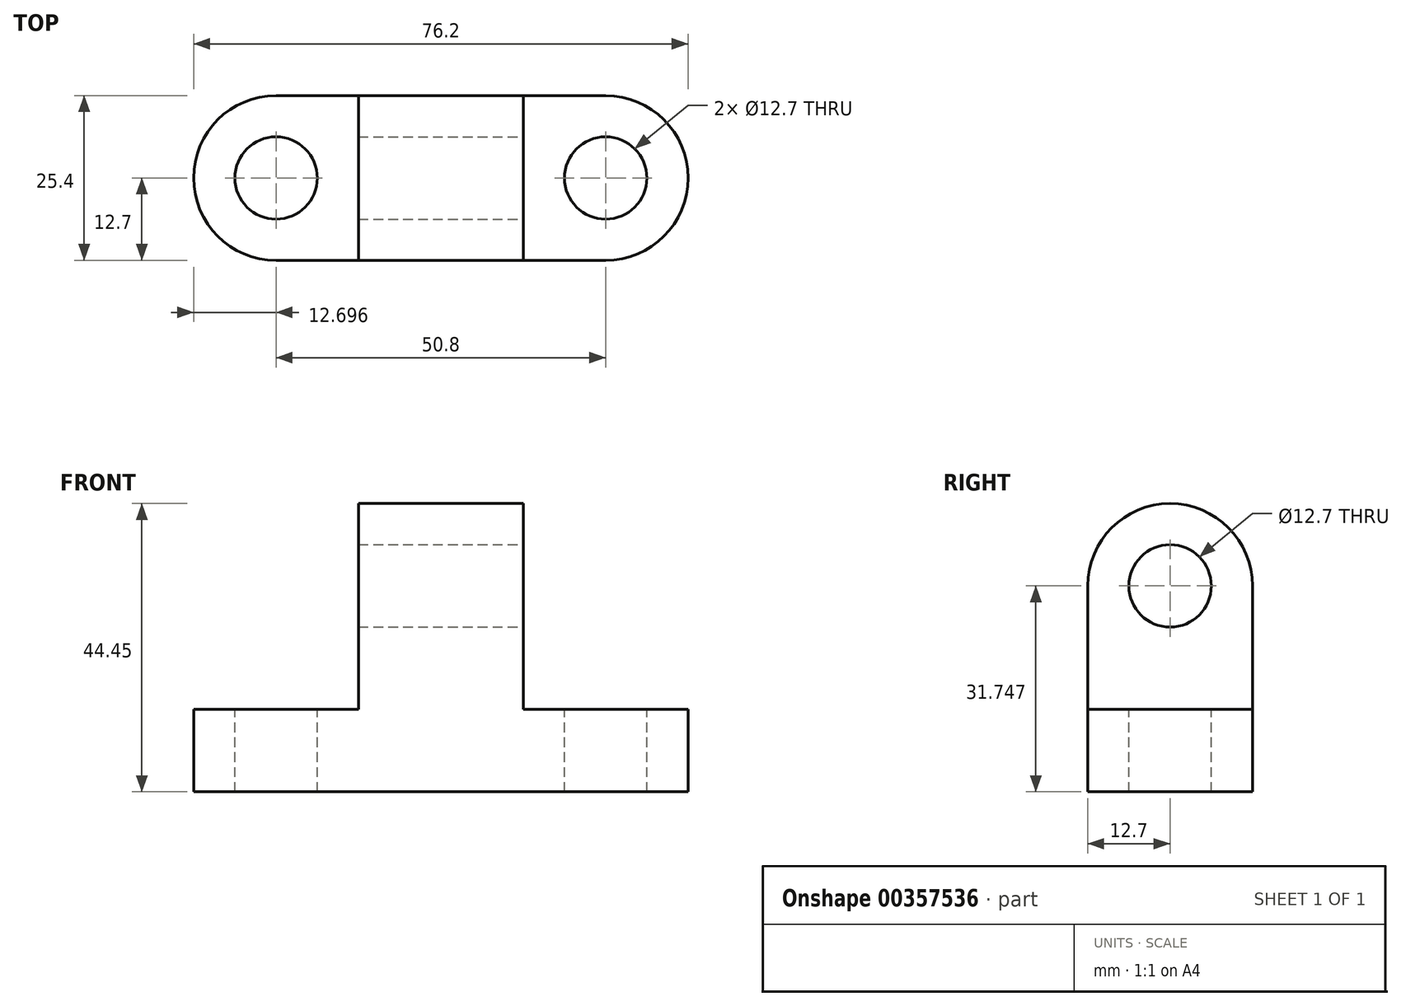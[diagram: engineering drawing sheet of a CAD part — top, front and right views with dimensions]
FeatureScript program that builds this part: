
annotation { "Feature Type Name" : "Feature", "Feature Type Description" : "" }
export const myFeature = defineFeature(function(context is Context, id is Id, definition is map)
    precondition{}
    {
        {
            var Q0;
            Q0=qCreatedBy(makeId("Front.planeOp"),FACE);
            var sketch = newSketch(context, id + "F0", { "sketchPlane" : qUnion([Q0])});
            skLineSegment(sketch, "E0", {"start": v(-50.66, -15.43) * mm, "end": v(-50.66, -28.13) * mm});
            skLineSegment(sketch, "E1", {"start": v(-50.66, -28.13) * mm, "end": v(0.14, -28.13) * mm});
            skLineSegment(sketch, "E2", {"start": v(0.14, -28.13) * mm, "end": v(0.14, -15.43) * mm});
            skLineSegment(sketch, "E3", {"start": v(0.14, -15.43) * mm, "end": v(-12.56, -15.43) * mm});
            skLineSegment(sketch, "E4", {"start": v(-12.56, -15.43) * mm, "end": v(-12.56, 3.62) * mm});
            skLineSegment(sketch, "E5", {"start": v(-12.56, 3.62) * mm, "end": v(-37.96, 3.62) * mm});
            skLineSegment(sketch, "E6", {"start": v(-37.96, 3.62) * mm, "end": v(-37.96, -15.43) * mm});
            skLineSegment(sketch, "E7", {"start": v(-37.96, -15.43) * mm, "end": v(-50.66, -15.43) * mm});
            skSolve(sketch);
        }
        {
            var Q0;
            Q0=makeQuery(id+"F0.imprint","IMPRINT",FACE,{"disambiguationData":[TD([[makeQuery(id+"F0.imprint","IMPRINT",EDGE,{"derivedFrom":sQuery(id+"F0.wireOp",EDGE,"E0")}),1.0]])]});
            extrude(context, id + "F1", {"entities" : qUnion([Q0]), "depth" : 25.4 * mm});
        }
        {
            var Q0;
            Q0=makeQuery(id+"F1.opExtrude","SWEPT_FACE",FACE,{"disambiguationData":[OSD([sQuery(id+"F0.wireOp",EDGE,"E7")])]});
            var sketch = newSketch(context, id + "F2", { "sketchPlane" : qUnion([Q0])});
            skLineSegment(sketch, "E8", {"start": v(0.14, 0) * mm, "end": v(0.14, -12.7) * mm});
            skLineSegment(sketch, "E9", {"start": v(0.14, -12.7) * mm, "end": v(0.14, -25.4) * mm});
            skLineSegment(sketch, "E10", {"start": v(0.14, -12.7) * mm, "end": v(12.84, -12.7) * mm});
            skArc(sketch, "E11", {"start": v(0.14, -25.4) * mm, "mid": v(12.84, -12.7) * mm, "end": v(0.14, 0) * mm});
            skLineSegment(sketch, "E12", {"start": v(-50.66, 0) * mm, "end": v(-50.66, -12.7) * mm});
            skLineSegment(sketch, "E13", {"start": v(-50.66, -12.7) * mm, "end": v(-50.66, -25.4) * mm});
            skLineSegment(sketch, "E14", {"start": v(-50.66, -12.7) * mm, "end": v(-63.36, -12.7) * mm});
            skArc(sketch, "E15", {"start": v(-50.66, 0) * mm, "mid": v(-63.36, -12.7) * mm, "end": v(-50.66, -25.4) * mm});
            skSolve(sketch);
        }
        {
            var Q0;
            Q0 = qSketchRegion(id + "F2", true);
            extrude(context, id + "F3", {"entities" : qUnion([Q0]), "operationType" : NewBodyOperationType.ADD, "oppositeDirection" : true, "depth" : 12.7 * mm});
        }
        {
            var Q0;
            Q0=makeQuery(id+"F1.opExtrude","SWEPT_FACE",FACE,{"disambiguationData":[OSD([sQuery(id+"F0.wireOp",EDGE,"E4")])]});
            var sketch = newSketch(context, id + "F4", { "sketchPlane" : qUnion([Q0])});
            skLineSegment(sketch, "E16", {"start": v(-25.4, 3.62) * mm, "end": v(-12.7, 3.62) * mm});
            skLineSegment(sketch, "E17", {"start": v(-12.7, 3.62) * mm, "end": v(0, 3.62) * mm});
            skLineSegment(sketch, "E18", {"start": v(-12.7, 3.62) * mm, "end": v(-12.7, 16.32) * mm});
            skArc(sketch, "E19", {"start": v(0, 3.62) * mm, "mid": v(-12.7, 16.32) * mm, "end": v(-25.4, 3.62) * mm});
            skSolve(sketch);
        }
        {
            var Q0;
            Q0 = qSketchRegion(id + "F4", true);
            extrude(context, id + "F5", {"entities" : qUnion([Q0]), "operationType" : NewBodyOperationType.ADD, "oppositeDirection" : true, "depth" : 25.4 * mm});
        }
        {
            var Q0;
            Q0=makeQuery(id+"F5.boolean.opBoolean","MERGE",FACE,{"derivedFrom":[makeQuery(id+"F1.opExtrude","SWEPT_FACE",FACE,{"disambiguationData":[OSD([sQuery(id+"F0.wireOp",EDGE,"E4")])]}),makeQuery(id+"F5.opExtrude","CAP_FACE",FACE,{"disambiguationData":[OSD([sQuery(id+"F4.wireOp",EDGE,"E16"),sQuery(id+"F4.wireOp",EDGE,"E17"),sQuery(id+"F4.wireOp",EDGE,"E19")])],"isStart":true})]});
            var sketch = newSketch(context, id + "F6", { "sketchPlane" : qUnion([Q0])});
            skLineSegment(sketch, "E20", {"start": v(-12.7, 16.32) * mm, "end": v(-12.7, 9.97) * mm});
            skPoint(sketch, "E20.endSnap0", {"position": v(-12.7, 16.32) * mm});
            skLineSegment(sketch, "E21", {"start": v(-25.4, 3.62) * mm, "end": v(-19.05, 3.62) * mm});
            skLineSegment(sketch, "E22", {"start": v(0, 3.62) * mm, "end": v(-6.35, 3.62) * mm});
            skCircle(sketch, "E23", {"center": v(-12.7, 3.62) * mm, "radius": 6.35 * mm});
            skSolve(sketch);
        }
        {
            var Q0;
            {var subQ0=sQuery(id+"F6.wireOp",EDGE,"E23");var subQ1=makeQuery(id+"F6.imprint","INTERSECT",VERTEX,{"derivedFrom":[sQuery(id+"F6.wireOp",EDGE,"E20"),subQ0]});Q0=makeQuery(id+"F6.imprint","IMPRINT",FACE,{"disambiguationData":[TD([[makeQuery(id+"F6.imprint","IMPRINT",EDGE,{"disambiguationData":[TD([[subQ1,1.0]])],"derivedFrom":subQ0}),1.0]])]});}
            extrude(context, id + "F7", {"entities" : qUnion([Q0]), "operationType" : NewBodyOperationType.REMOVE, "oppositeDirection" : true, "depth" : 25.4 * mm});
        }
        {
            var Q0;
            Q0=makeQuery(id+"F3.boolean.opBoolean","MERGE",FACE,{"derivedFrom":[makeQuery(id+"F1.opExtrude","SWEPT_FACE",FACE,{"disambiguationData":[OSD([sQuery(id+"F0.wireOp",EDGE,"E7")])]}),makeQuery(id+"F3.opExtrude","CAP_FACE",FACE,{"disambiguationData":[OSD([sQuery(id+"F2.wireOp",EDGE,"E12"),sQuery(id+"F2.wireOp",EDGE,"E13"),sQuery(id+"F2.wireOp",EDGE,"E15")])],"isStart":true})]});
            var sketch = newSketch(context, id + "F8", { "sketchPlane" : qUnion([Q0])});
            skLineSegment(sketch, "E24", {"start": v(0.14, 0) * mm, "end": v(0.14, -6.35) * mm});
            skLineSegment(sketch, "E25", {"start": v(0.14, -25.4) * mm, "end": v(0.14, -19.05) * mm});
            skLineSegment(sketch, "E26", {"start": v(12.84, -12.7) * mm, "end": v(6.49, -12.7) * mm});
            skLineSegment(sketch, "E27", {"start": v(-50.66, 0) * mm, "end": v(-50.66, -6.35) * mm});
            skLineSegment(sketch, "E28", {"start": v(-63.36, -12.7) * mm, "end": v(-57.01, -12.7) * mm});
            skLineSegment(sketch, "E29", {"start": v(-50.66, -25.4) * mm, "end": v(-50.66, -19.05) * mm});
            skCircle(sketch, "E30", {"center": v(-50.66, -12.7) * mm, "radius": 6.35 * mm});
            skCircle(sketch, "E31", {"center": v(0.14, -12.7) * mm, "radius": 6.35 * mm});
            skSolve(sketch);
        }
        {
            var Q0;
            {var subQ0=sQuery(id+"F8.wireOp",EDGE,"E30");var subQ1=makeQuery(id+"F8.imprint","INTERSECT",VERTEX,{"derivedFrom":[sQuery(id+"F8.wireOp",EDGE,"E27"),subQ0]});Q0=makeQuery(id+"F8.imprint","IMPRINT",FACE,{"disambiguationData":[TD([[makeQuery(id+"F8.imprint","IMPRINT",EDGE,{"disambiguationData":[TD([[subQ1,-1.0]])],"derivedFrom":subQ0}),1.0]])]});}
            var Q1;
            {var subQ0=sQuery(id+"F8.wireOp",EDGE,"E31");var subQ1=makeQuery(id+"F8.imprint","IMPRINT",VERTEX,{"disambiguationData":[OD(0.0)],"derivedFrom":subQ0});Q1=makeQuery(id+"F8.imprint","IMPRINT",FACE,{"disambiguationData":[TD([[makeQuery(id+"F8.imprint","IMPRINT",EDGE,{"disambiguationData":[TD([[subQ1,1.0]])],"derivedFrom":subQ0}),1.0]])]});}
            extrude(context, id + "F9", {"entities" : qUnion([Q0, Q1]), "operationType" : NewBodyOperationType.REMOVE, "oppositeDirection" : true, "depth" : 12.7 * mm});
        }
    });
